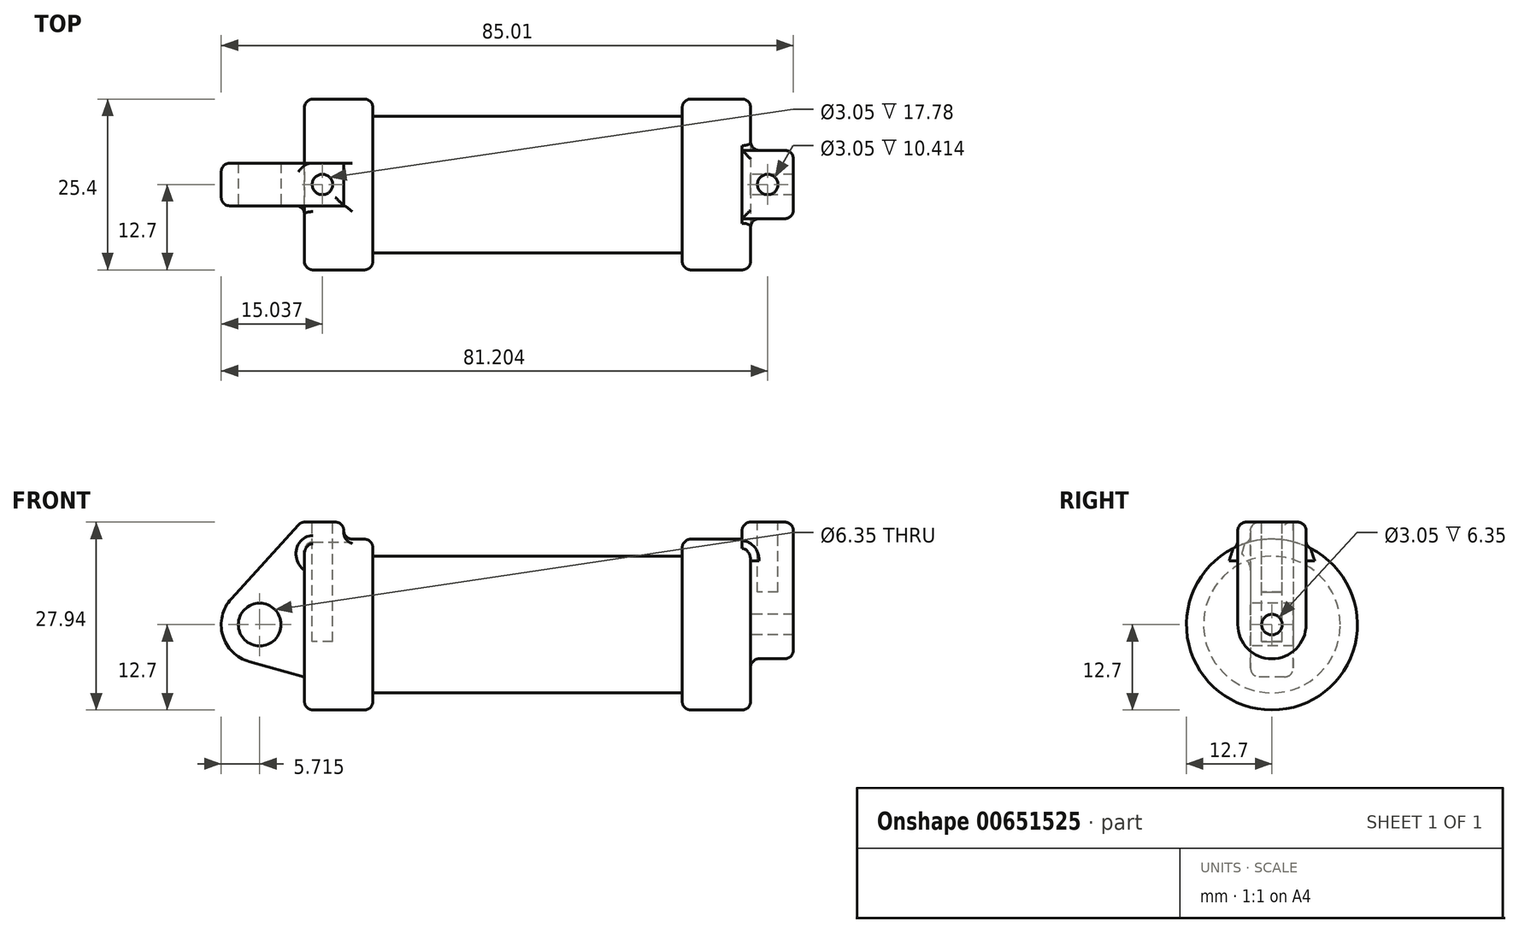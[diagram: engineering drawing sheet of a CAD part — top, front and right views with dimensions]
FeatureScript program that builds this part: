
annotation { "Feature Type Name" : "Feature", "Feature Type Description" : "" }
export const myFeature = defineFeature(function(context is Context, id is Id, definition is map)
    precondition{}
    {
        {
            var Q0;
            Q0=qCreatedBy(makeId("Front.planeOp"),FACE);
            var sketch = newSketch(context, id + "F0", { "sketchPlane" : qUnion([Q0])});
            skLineSegment(sketch, "E0", {"start": v(0, 0) * mm, "end": v(0, 12.7) * mm});
            skLineSegment(sketch, "E1", {"start": v(0, 12.7) * mm, "end": v(10.16, 12.7) * mm});
            skLineSegment(sketch, "E2", {"start": v(10.16, 12.7) * mm, "end": v(10.16, 10.16) * mm});
            skLineSegment(sketch, "E3", {"start": v(10.16, 10.16) * mm, "end": v(56.13, 10.16) * mm});
            skLineSegment(sketch, "E4", {"start": v(56.13, 10.16) * mm, "end": v(56.13, 12.7) * mm});
            skLineSegment(sketch, "E5", {"start": v(56.13, 12.7) * mm, "end": v(66.3, 12.7) * mm});
            skLineSegment(sketch, "E6", {"start": v(66.3, 12.7) * mm, "end": v(66.3, 0) * mm});
            skLineSegment(sketch, "E7", {"start": v(66.3, 0) * mm, "end": v(0, 0) * mm});
            skLineSegment(sketch, "E8", {"start": v(5.84, 15.24) * mm, "end": v(-0.5, 15.24) * mm});
            skLineSegment(sketch, "E9", {"start": v(-0.5, 15.24) * mm, "end": v(-10.88, 3.85) * mm});
            skLineSegment(sketch, "E10", {"start": v(0, 0) * mm, "end": v(-6.65, 0) * mm});
            skCircle(sketch, "E11", {"center": v(-6.65, 0) * mm, "radius": 5.72 * mm});
            skCircle(sketch, "E12", {"center": v(-6.65, 0) * mm, "radius": 3.18 * mm});
            skLineSegment(sketch, "E13", {"start": v(5.84, 15.24) * mm, "end": v(5.84, -9.4) * mm});
            skLineSegment(sketch, "E14", {"start": v(5.84, -9.4) * mm, "end": v(-8.18, -5.5) * mm});
            skSolve(sketch);
        }
        {
            var Q0;
            {var subQ0=sQuery(id+"F0.wireOp",EDGE,"E2");Q0=makeQuery(id+"F0.imprint","IMPRINT",FACE,{"disambiguationData":[TD([[makeQuery(id+"F0.imprint","IMPRINT",EDGE,{"derivedFrom":subQ0}),-1.0]])]});}
            var Q1;
            {var subQ0=sQuery(id+"F0.wireOp",EDGE,"E0");Q1=makeQuery(id+"F0.imprint","IMPRINT",FACE,{"disambiguationData":[TD([[makeQuery(id+"F0.imprint","IMPRINT",EDGE,{"derivedFrom":subQ0}),-1.0]])]});}
            var Q2;
            Q2=sQuery(id+"F0.wireOp",EDGE,"E10");
            revolve(context, id + "F1", {"entities" : qUnion([Q0, Q1]), "axis" : qUnion([Q2]), "revolveType" : RevolveType.FULL});
        }
        {
            var Q0;
            {var subQ0=sQuery(id+"F0.wireOp",EDGE,"E0");Q0=makeQuery(id+"F0.imprint","IMPRINT",FACE,{"disambiguationData":[TD([[makeQuery(id+"F0.imprint","IMPRINT",EDGE,{"derivedFrom":subQ0}),-1.0]])]});}
            var Q1;
            {var subQ0=sQuery(id+"F0.wireOp",EDGE,"E14");Q1=makeQuery(id+"F0.imprint","IMPRINT",FACE,{"disambiguationData":[TD([[makeQuery(id+"F0.imprint","IMPRINT",EDGE,{"derivedFrom":subQ0}),-1.0]])]});}
            var Q2;
            {var subQ1=sQuery(id+"F0.wireOp",EDGE,"E0");Q2=makeQuery(id+"F0.imprint","IMPRINT",FACE,{"disambiguationData":[TD([[makeQuery(id+"F0.imprint","IMPRINT",EDGE,{"derivedFrom":subQ1}),1.0]])]});}
            var Q3;
            {var subQ5=sQuery(id+"F0.wireOp",EDGE,"E12");Q3=makeQuery(id+"F0.imprint","IMPRINT",FACE,{"disambiguationData":[TD([[makeQuery(id+"F0.imprint","IMPRINT",EDGE,{"derivedFrom":subQ5}),-1.0]])]});}
            extrude(context, id + "F2", {"entities" : qUnion([Q0, Q1, Q2, Q3]), "operationType" : NewBodyOperationType.ADD, "endBound" : BoundingType.SYMMETRIC, "oppositeDirection" : true, "depth" : 6.35 * mm, "offsetDistance" : 25.4 * mm});
        }
        {
            var Q0;
            Q0=makeQuery(id+"F1.opRevolve","SWEPT_FACE",FACE,{"disambiguationData":[OSD([sQuery(id+"F0.wireOp",EDGE,"E6")])]});
            var sketch = newSketch(context, id + "F3", { "sketchPlane" : qUnion([Q0])});
            skCircle(sketch, "E15", {"center": v(0, 0) * mm, "radius": 1.52 * mm});
            skCircle(sketch, "E16", {"center": v(0, 0) * mm, "radius": 5.08 * mm});
            skLineSegment(sketch, "E17", {"start": v(-5.08, 0) * mm, "end": v(-5.08, 15.24) * mm});
            skLineSegment(sketch, "E18", {"start": v(-5.08, 15.24) * mm, "end": v(5.08, 15.24) * mm});
            skLineSegment(sketch, "E19", {"start": v(5.08, 0) * mm, "end": v(5.08, 15.24) * mm});
            skSolve(sketch);
        }
        {
            var Q0;
            {var subQ0=sQuery(id+"F3.wireOp",EDGE,"E18");Q0=makeQuery(id+"F3.imprint","IMPRINT",FACE,{"disambiguationData":[TD([[makeQuery(id+"F3.imprint","IMPRINT",EDGE,{"derivedFrom":subQ0}),-1.0]])]});}
            var Q1;
            {var subQ0=sQuery(id+"F3.wireOp",EDGE,"E17");var subQ1=sQuery(id+"F3.wireOp",EDGE,"E16");var subQ2=makeQuery(id+"F3.imprint","INTERSECT",VERTEX,{"derivedFrom":[subQ1,subQ0]});Q1=makeQuery(id+"F3.imprint","IMPRINT",FACE,{"disambiguationData":[TD([[makeQuery(id+"F3.imprint","IMPRINT",EDGE,{"disambiguationData":[TD([[subQ2,1.0]])],"derivedFrom":subQ1}),-1.0]])]});}
            var Q2;
            Q2=makeQuery(id+"F3.imprint","IMPRINT",FACE,{"disambiguationData":[TD([[makeQuery(id+"F3.imprint","IMPRINT",EDGE,{"derivedFrom":sQuery(id+"F3.wireOp",EDGE,"E15")}),-1.0]])]});
            extrude(context, id + "F4", {"entities" : qUnion([Q0, Q1, Q2]), "operationType" : NewBodyOperationType.ADD, "depth" : 6.35 * mm, "offsetDistance" : 25.4 * mm, "hasSecondDirection" : true, "secondDirectionOppositeDirection" : true, "secondDirectionDepth" : 1.27 * mm});
        }
        {
            var Q0;
            Q0=makeQuery(id+"F2.opExtrude","SWEPT_FACE",FACE,{"disambiguationData":[OSD([sQuery(id+"F0.wireOp",EDGE,"E8")])]});
            var sketch = newSketch(context, id + "F5", { "sketchPlane" : qUnion([Q0])});
            skLineSegment(sketch, "E20", {"start": v(2.67, 3.18) * mm, "end": v(2.67, -3.18) * mm, "construction": true});
            skLineSegment(sketch, "E21", {"start": v(-0.5, 0) * mm, "end": v(5.84, 0) * mm, "construction": true});
            skCircle(sketch, "E22", {"center": v(2.67, 0) * mm, "radius": 1.52 * mm});
            skSolve(sketch);
        }
        {
            var Q0;
            Q0=makeQuery(id+"F5.imprint","IMPRINT",FACE,{"disambiguationData":[TD([[makeQuery(id+"F5.imprint","IMPRINT",EDGE,{"derivedFrom":sQuery(id+"F5.wireOp",EDGE,"E22")}),1.0]])]});
            var Q1;
            Q1=sQuery(id+"F5.wireOp",EDGE,"E22");
            extrude(context, id + "F6", {"entities" : qUnion([Q0]), "operationType" : NewBodyOperationType.REMOVE, "surfaceEntities" : qUnion([Q1]), "oppositeDirection" : true, "depth" : 17.78 * mm, "offsetDistance" : 25.4 * mm});
        }
        {
            var Q0;
            Q0=makeQuery(id+"F4.opExtrude","SWEPT_FACE",FACE,{"disambiguationData":[OSD([sQuery(id+"F3.wireOp",EDGE,"E18")])]});
            var sketch = newSketch(context, id + "F7", { "sketchPlane" : qUnion([Q0])});
            skLineSegment(sketch, "E23", {"start": v(68.83, 5.08) * mm, "end": v(68.83, -5.08) * mm, "construction": true});
            skLineSegment(sketch, "E24", {"start": v(65.02, 0) * mm, "end": v(72.64, 0) * mm, "construction": true});
            skCircle(sketch, "E25", {"center": v(68.83, 0) * mm, "radius": 1.52 * mm});
            skSolve(sketch);
        }
        {
            var Q0;
            Q0=makeQuery(id+"F7.imprint","IMPRINT",FACE,{"disambiguationData":[TD([[makeQuery(id+"F7.imprint","IMPRINT",EDGE,{"derivedFrom":sQuery(id+"F7.wireOp",EDGE,"E25")}),1.0]])]});
            var Q1;
            Q1=sQuery(id+"F7.wireOp",EDGE,"E25");
            extrude(context, id + "F8", {"entities" : qUnion([Q0]), "operationType" : NewBodyOperationType.REMOVE, "surfaceEntities" : qUnion([Q1]), "oppositeDirection" : true, "depth" : 10.4 * mm, "offsetDistance" : 25.4 * mm});
        }
        {
            var Q0;
            Q0=makeQuery(id+"F1.opRevolve","SWEPT_EDGE",EDGE,{"disambiguationData":[OSD([sQuery(id+"F0.wireOp",EDGE,"E0"),sQuery(id+"F0.wireOp",EDGE,"E1")])]});
            var Q1;
            Q1=makeQuery(id+"F1.opRevolve","SWEPT_EDGE",EDGE,{"disambiguationData":[OSD([sQuery(id+"F0.wireOp",EDGE,"E1"),sQuery(id+"F0.wireOp",EDGE,"E2")])]});
            var Q2;
            Q2=makeQuery(id+"F1.opRevolve","SWEPT_EDGE",EDGE,{"disambiguationData":[OSD([sQuery(id+"F0.wireOp",EDGE,"E4"),sQuery(id+"F0.wireOp",EDGE,"E5")])]});
            var Q3;
            Q3=makeQuery(id+"F1.opRevolve","SWEPT_EDGE",EDGE,{"disambiguationData":[OSD([sQuery(id+"F0.wireOp",EDGE,"E5"),sQuery(id+"F0.wireOp",EDGE,"E6")])]});
            var Q4;
            Q4=makeQuery(id+"F2.opExtrude","CAP_EDGE",EDGE,{"disambiguationData":[OSD([sQuery(id+"F0.wireOp",EDGE,"E8")])],"isStart":true});
            var Q5;
            Q5=makeQuery(id+"F2.opExtrude","SWEPT_EDGE",EDGE,{"disambiguationData":[OSD([sQuery(id+"F0.wireOp",EDGE,"E8"),sQuery(id+"F0.wireOp",EDGE,"E13")])]});
            var Q6;
            Q6=makeQuery(id+"F2.boolean.opBoolean","INTERSECT",EDGE,{"derivedFrom":[makeQuery(id+"F1.opRevolve","SWEPT_FACE",FACE,{"disambiguationData":[OSD([sQuery(id+"F0.wireOp",EDGE,"E1")])]}),makeQuery(id+"F2.opExtrude","SWEPT_FACE",FACE,{"disambiguationData":[OSD([sQuery(id+"F0.wireOp",EDGE,"E13")])]})]});
            var Q7;
            Q7=makeQuery(id+"F2.boolean.opBoolean","INTERSECT",EDGE,{"derivedFrom":[makeQuery(id+"F1.opRevolve","SWEPT_FACE",FACE,{"disambiguationData":[OSD([sQuery(id+"F0.wireOp",EDGE,"E1")])]}),makeQuery(id+"F2.opExtrude","CAP_FACE",FACE,{"disambiguationData":[OSD([sQuery(id+"F0.wireOp",EDGE,"E8"),sQuery(id+"F0.wireOp",EDGE,"E9"),sQuery(id+"F0.wireOp",EDGE,"E11"),sQuery(id+"F0.wireOp",EDGE,"E12"),sQuery(id+"F0.wireOp",EDGE,"E13"),sQuery(id+"F0.wireOp",EDGE,"E14")])],"isStart":true})]});
            var Q8;
            Q8=makeQuery(id+"F2.opExtrude","CAP_EDGE",EDGE,{"disambiguationData":[OSD([sQuery(id+"F0.wireOp",EDGE,"E9")])],"isStart":true});
            var Q9;
            Q9=makeQuery(id+"F2.opExtrude","SWEPT_EDGE",EDGE,{"disambiguationData":[OSD([sQuery(id+"F0.wireOp",EDGE,"E8"),sQuery(id+"F0.wireOp",EDGE,"E9")])]});
            var Q10;
            Q10=makeQuery(id+"F2.opExtrude","CAP_EDGE",EDGE,{"disambiguationData":[OSD([sQuery(id+"F0.wireOp",EDGE,"E14")])],"isStart":false});
            var Q11;
            Q11=makeQuery(id+"F4.opExtrude","CAP_EDGE",EDGE,{"disambiguationData":[OSD([sQuery(id+"F3.wireOp",EDGE,"E18")])],"isStart":false});
            var Q12;
            Q12=makeQuery(id+"F4.opExtrude","SWEPT_EDGE",EDGE,{"disambiguationData":[OSD([sQuery(id+"F3.wireOp",EDGE,"E18"),sQuery(id+"F3.wireOp",EDGE,"E19")])]});
            var Q13;
            Q13=makeQuery(id+"F4.opExtrude","CAP_EDGE",EDGE,{"disambiguationData":[OSD([sQuery(id+"F3.wireOp",EDGE,"E18")])],"isStart":true});
            var Q14;
            Q14=makeQuery(id+"F4.opExtrude","SWEPT_EDGE",EDGE,{"disambiguationData":[OSD([sQuery(id+"F3.wireOp",EDGE,"E17"),sQuery(id+"F3.wireOp",EDGE,"E18")])]});
            var Q15;
            Q15=makeQuery(id+"F4.opExtrude","CAP_EDGE",EDGE,{"disambiguationData":[OSD([sQuery(id+"F3.wireOp",EDGE,"E17")])],"isStart":false});
            var Q16;
            Q16=makeQuery(id+"F4.opExtrude","CAP_EDGE",EDGE,{"disambiguationData":[OSD([sQuery(id+"F3.wireOp",EDGE,"E16")])],"isStart":false});
            var Q17;
            Q17=makeQuery(id+"F4.boolean.opBoolean","INTERSECT",EDGE,{"derivedFrom":[makeQuery(id+"F1.opRevolve","SWEPT_FACE",FACE,{"disambiguationData":[OSD([sQuery(id+"F0.wireOp",EDGE,"E6")])]}),makeQuery(id+"F4.opExtrude","SWEPT_FACE",FACE,{"disambiguationData":[OSD([sQuery(id+"F3.wireOp",EDGE,"E19")])]})]});
            var Q18;
            Q18=makeQuery(id+"F4.boolean.opBoolean","INTERSECT",EDGE,{"derivedFrom":[makeQuery(id+"F1.opRevolve","SWEPT_FACE",FACE,{"disambiguationData":[OSD([sQuery(id+"F0.wireOp",EDGE,"E5")])]}),makeQuery(id+"F4.opExtrude","SWEPT_FACE",FACE,{"disambiguationData":[OSD([sQuery(id+"F3.wireOp",EDGE,"E17")])]})]});
            fillet(context, id + "F9", {"entities" : qUnion([Q0, Q1, Q2, Q3, Q4, Q5, Q6, Q7, Q8, Q9, Q10, Q11, Q12, Q13, Q14, Q15, Q16, Q17, Q18]), "radius" : 1.27 * mm, "tangentPropagation" : true, "allowEdgeOverflow" : false});
        }
    });
